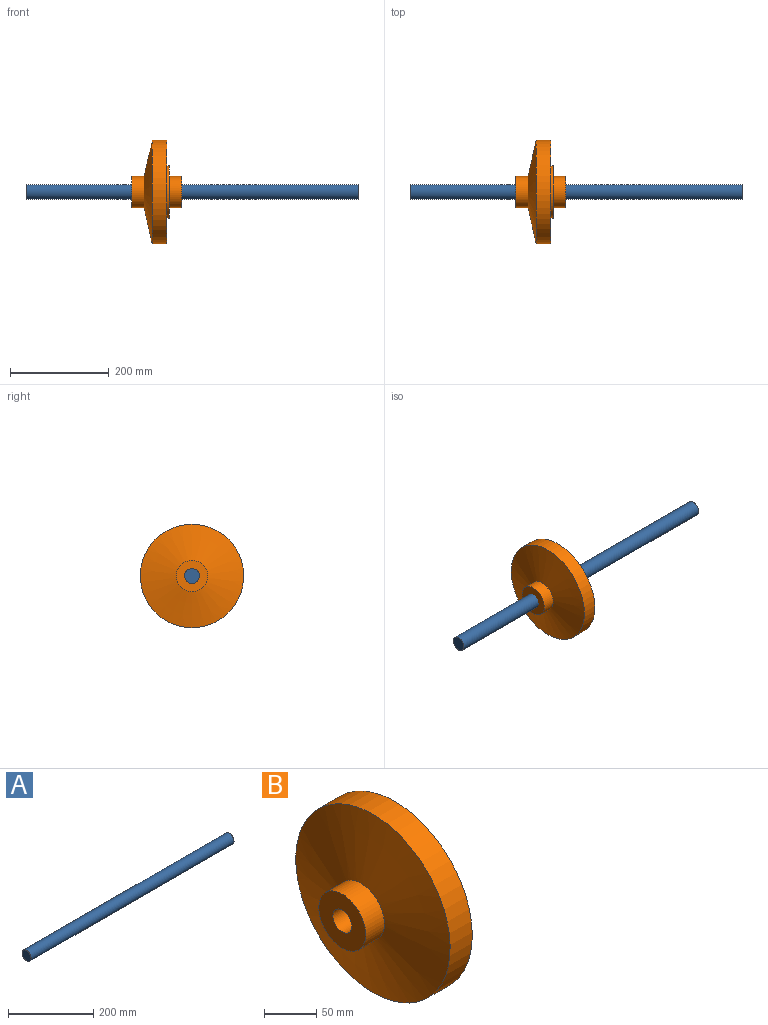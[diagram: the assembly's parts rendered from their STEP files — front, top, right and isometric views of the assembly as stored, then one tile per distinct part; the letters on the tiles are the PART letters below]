
ASSEMBLY  parts=2 mates=1
PART A: 3 faces, bbox 673.1x30.1x30.1 mm
  f0: plane 30.12x30.12mm, normal (1,0,0), area 712.7mm2, adj f1
  f1: cylinder r=15.06mm len=673.1mm, axis (-1,0,0), area 63701.2mm2, adj f0,f2
  f2: plane 30.12x30.12mm, normal (-1,0,0), area 712.7mm2, adj f1
PART B: 10 faces, bbox 101.6x209.6x209.6 mm
  f0: cylinder r=104.77mm len=209.55mm, axis (1,0,0), area 19748.5mm2, adj f1,f9
  f1: cone r=104.77mm half-angle=77.5deg, axis (1,0,0), area 32082.6mm2, adj f0,f2
  f2: cylinder r=31.75mm len=63.5mm, axis (1,0,0), area 5067.1mm2, adj f1,f3
  f3: plane 63.5x63.5mm, normal (-1,0,0), area 2660.2mm2, adj f2,f4
  f4: cylinder r=12.7mm len=101.6mm, axis (1,0,0), area 8107.3mm2, adj f3,f5
  f5: plane 63.5x63.5mm, normal (1,0,0), area 2660.2mm2, adj f4,f6
  f6: cylinder r=31.75mm len=63.5mm, axis (1,0,0), area 5067.1mm2, adj f5,f7
  f7: plane 106.95x106.95mm, normal (1,0,0), area 5817.4mm2, adj f6,f8
  f8: cylinder r=53.48mm len=106.95mm, axis (1,0,0), area 1545mm2, adj f7,f9
  f9: plane 209.55x209.55mm, normal (1,0,0), area 25503.5mm2, adj f0,f8
PLACE A t=(-168.04,19.56,-44.25)mm
PLACE B t=(34.17,19.56,-44.25)mm
MATE planar B.f0 <-> A.f1  axis (1,0,0) through (34.17,19.56,-44.25)mm
